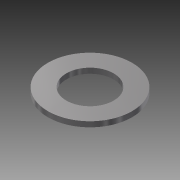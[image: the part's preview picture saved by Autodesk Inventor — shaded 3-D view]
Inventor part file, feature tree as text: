
AUTODESK INVENTOR PART (.ipt)
format: ipt  version: 2013 (Build 170138000, 138)  size: 79,872 bytes
history: native  units: mm
features: other x1, extrude x1, sketch x1
ambient origin geometry x1: Origin
feature tree (3):
  other  "ソリッド1"
  extrude  "押し出し1"  Depth=4.5mm
  sketch  "スケッチ1"
